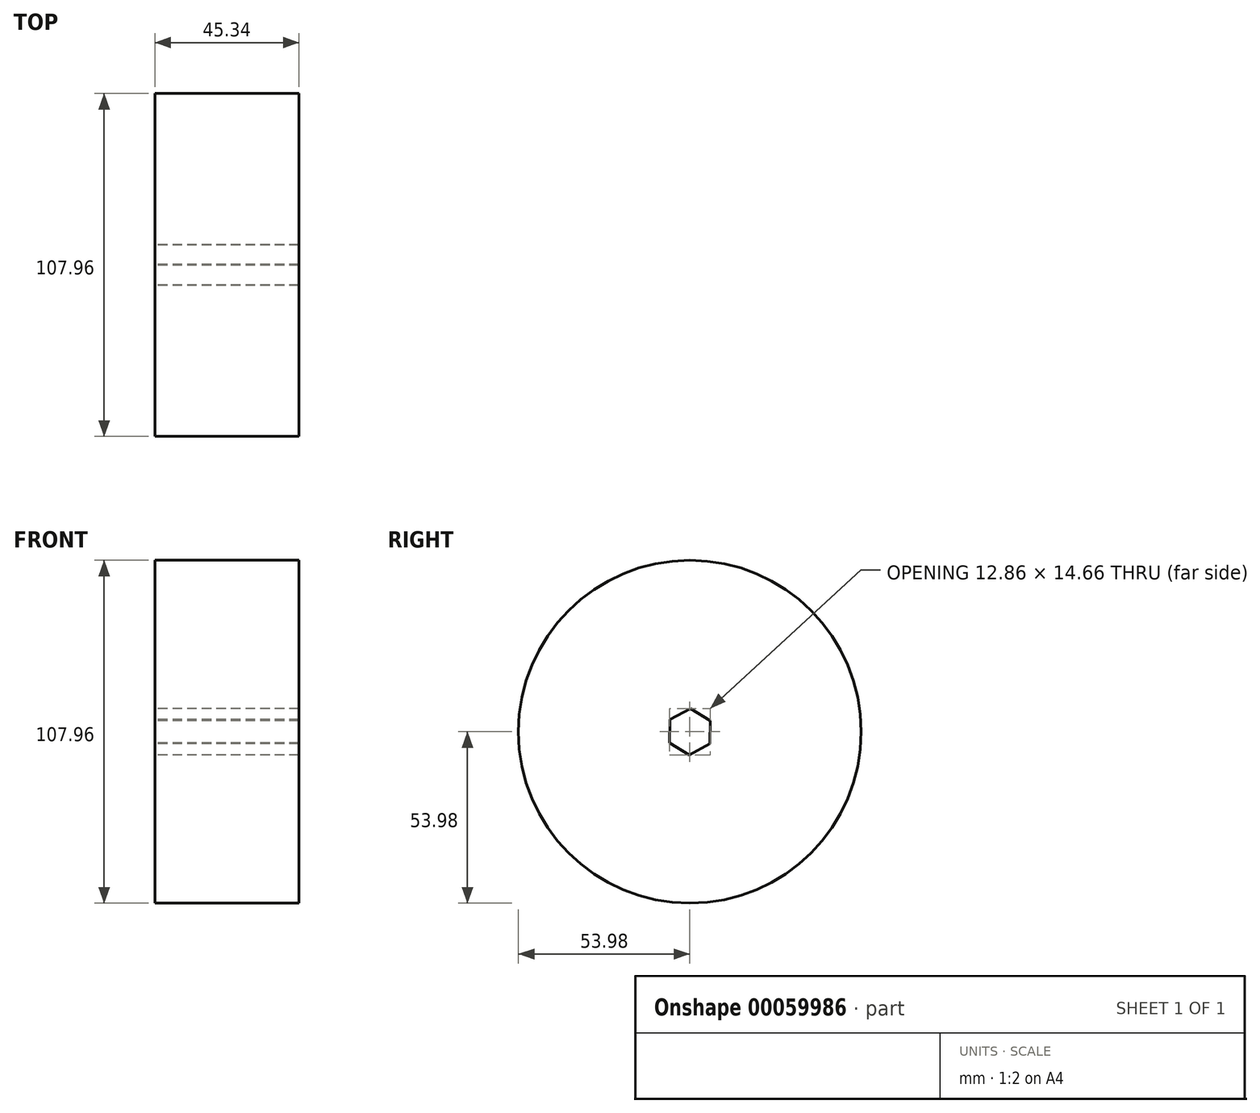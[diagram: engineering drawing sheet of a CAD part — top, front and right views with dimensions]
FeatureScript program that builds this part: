
annotation { "Feature Type Name" : "Feature", "Feature Type Description" : "" }
export const myFeature = defineFeature(function(context is Context, id is Id, definition is map)
    precondition{}
    {
        {
            var Q0;
            Q0=qCreatedBy(makeId("Right.planeOp"),FACE);
            var sketch = newSketch(context, id + "F0", { "sketchPlane" : qUnion([Q0])});
            skCircle(sketch, "E0", {"center": v(0, 0) * mm, "radius": 53.98 * mm});
            skCircle(sketch, "E1.cCircle", {"center": v(0, 0) * mm, "radius": 6.35 * mm, "construction": true});
            skLineSegment(sketch, "E1.0", {"start": v(0.17, 7.33) * mm, "end": v(6.43, 3.52) * mm});
            skLineSegment(sketch, "E1.1", {"start": v(6.43, 3.52) * mm, "end": v(6.26, -3.81) * mm});
            skLineSegment(sketch, "E1.2", {"start": v(6.26, -3.81) * mm, "end": v(-0.17, -7.33) * mm});
            skLineSegment(sketch, "E1.3", {"start": v(-0.17, -7.33) * mm, "end": v(-6.43, -3.52) * mm});
            skLineSegment(sketch, "E1.4", {"start": v(-6.43, -3.52) * mm, "end": v(-6.26, 3.81) * mm});
            skLineSegment(sketch, "E1.5", {"start": v(-6.26, 3.81) * mm, "end": v(0.17, 7.33) * mm});
            skPoint(sketch, "E1.0.midPoint", {"position": v(3.3, 5.43) * mm});
            skSolve(sketch);
        }
        {
            var Q0;
            Q0=makeQuery(id+"F0.imprint","IMPRINT",FACE,{"disambiguationData":[TD([[makeQuery(id+"F0.imprint","IMPRINT",EDGE,{"derivedFrom":sQuery(id+"F0.wireOp",EDGE,"E0")}),1.0]])]});
            extrude(context, id + "F1", {"entities" : qUnion([Q0]), "depth" : 45.34 * mm});
        }
    });
